# Revit family: Брейк
name_source: partatom
category: Осветительные приборы
units: mm (PartAtom-declared; Revit-internal decimal feet)

## family parameters
Всегда вертикально = Да
Источник света = Да
На основе рабочей плоскости = Нет
Общий = Нет
При загрузке вырезать с полостями = Нет
Размер круглого соединителя = Использовать диаметр
Тип детали = Нормальный
Точка расчета площади = Нет

## types (2) — shared parameters
ADSK_URL страницы изделия = https://www.allfresco.ru
ADSK_Единица измерения = шт.
ADSK_Завод-изготовитель = ALFRESCO
ADSK_Количество фаз = 2
ADSK_Модель = Брейк ДТУ-159-AF
ADSK_Напряжение = 220 В
ADSK_Полная мощность = 0 В·А
ADSK_Размер_Высота = 4500 мм
ADSK_Ток = 0 А
ADSK_Энергоэффективность = 110 лм/Вт
H1 = 8 мм
H2 = 2097 мм
H3 = 4055 мм
H4 = 4479 мм
H_конечной точки = 1500 мм
IP Class = IP 67
L_отступ до конечной точки = 1500 мм
L_отступ до центра = 1000 мм
S1 = 114 мм
a1 = 180 мм
a2 = 240 мм
l_отверстия = 20 мм
r_скругление фасонки = 15 мм
s_отверстия = 9 мм
x1 = 10 мм
x2 = 30 мм
Блок аварийного питания = Нет
Класс защиты = 1
Класс пожароопасности = F (светильники предназначены для установки непосредственно на поверхность из нормально воспламеняемых материалов)
Климатическая зона = УХЛ1
Короб_Диаметр = 20 мм
Корпус светильника = Антрацит
Материал рассеивателя = Светотехнический ПК
Область использования = Парки, скверы, общественные пространства, городская инфраструктура
Полная установленная мощность = 0 В·А
Рассеиватель = Белый_светодиод
Светофильтр = 16777215
Смещение цветовой температуры при затухании лампы = <Нет>
Таблица выбора = Таблица параметров светильников_par2
Температура эксплуатации = -40 +50
Тип ИС = LED-модуль
Тип КСС = тип ШБ (широкая боковая)
Тип ПРА = -
Тип продукции = LED-светильник
Угол наклона = 60.00°
Цветоывая температура = 2700-5500
zero-valued in all types: ADSK_Количество фаз числовое, ADSK_Коэффициент мощности

## per-type parameters (varying)
| type | 60вт | ADSK_Артикул | ADSK_Масса | ADSK_Масса_Текст | ADSK_Номинальная мощность | ADSK_Фактическая мощность | Файл фотометрической сетки |
| ДТУ159с1 Светодиодный светильник Брейк ДТУ-159-AF-30Вт-4.5 | Нет | ДТУ159с1 | 41 | 41 | 30 Вт | 29 Вт | DTU-159-AF Break 30W 150х70 2700K.ies |
| ДТУ159с2 Светодиодный светильник Брейк ДТУ-159-AF-60Вт-4.5 | Да | ДТУ159с2 | 43 | 43 | 60 Вт | 58 Вт | DTU-159-AF Break 60W 150х70 2700K.ies |

note: column(s) folded — value = type name in every type: ADSK_Наименование
